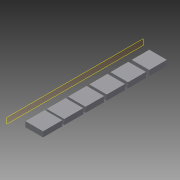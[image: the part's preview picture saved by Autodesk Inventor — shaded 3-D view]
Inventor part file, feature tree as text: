
AUTODESK INVENTOR PART (.ipt)
format: ipt  version: 2013 (Build 170138000, 138)  size: 190,464 bytes
history: native  units: mm
features: projected_geometry x9, extrude x5, sketch x5, pattern_linear x1, plane x1, mirror x1
ambient origin geometry x8: Origin, YZ Plane, XZ Plane, XY Plane, X Axis, Y Axis, Z Axis, Center Point
bodies: Solid1 (feature_tree)
feature tree (22):
  extrude  "Extrusion1"  Depth=10.0mm
  pattern_linear  "Rectangular Pattern1"  Count1=6 Spacing1=12.0mm
  extrude  "Extrusion2"  Depth=10.0mm
  plane  "Work Plane1"
  mirror  "Mirror1"
  extrude  "Extrusion3"  Depth=10.2mm
  extrude  "Extrusion4"  Depth=10.4mm
  extrude  "Extrusion5"  Depth=5.2mm
  sketch  "Sketch1"  dims[d0=10.0mm d2=10.0mm]
  sketch  "Sketch2"  dims[d3=3.0mm d4=0.0mm d5=60.0mm d7=12.0mm]
  projected_geometry  "Projected Loop1"
  projected_geometry  "Projected Loop2"
  projected_geometry  "Projected Loop3"
  projected_geometry  "Projected Loop4"
  projected_geometry  "Projected Loop5"
  sketch  "Sketch3"  dims[d8=12.0mm d10=10.0mm]
  projected_geometry  "Projected Loop6"
  projected_geometry  "Projected Loop7"
  sketch  "Sketch4"  dims[d11=10.0mm d12=10.2mm]
  projected_geometry  "Projected Loop8"
  sketch  "Sketch5"  dims[d13=5.1mm d14=10.4mm d15=5.2mm d16=5.3mm d17=5.4mm d18=10.6mm d19=10.8mm d20=11.0mm d21=5.5mm d22=3.0mm d23=0.0mm d24=3.0mm d25=0.0mm d26=3.0mm d27=0.0mm d28=3.0mm d29=0.0mm]
  projected_geometry  "Projected Loop9"
